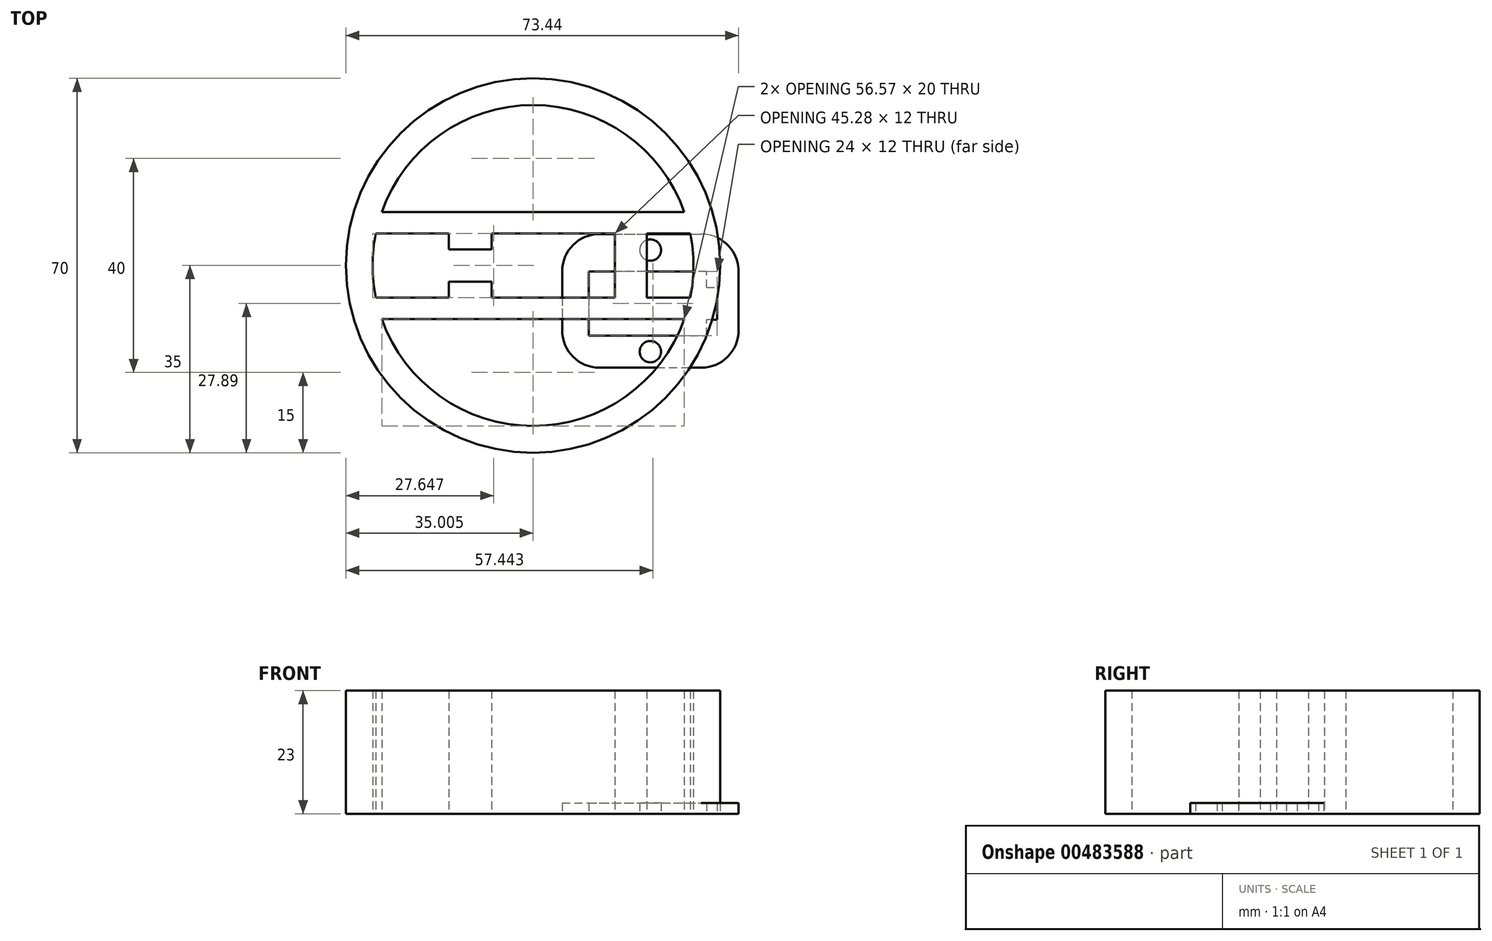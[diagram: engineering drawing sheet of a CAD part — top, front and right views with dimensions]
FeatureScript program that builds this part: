
annotation { "Feature Type Name" : "Feature", "Feature Type Description" : "" }
export const myFeature = defineFeature(function(context is Context, id is Id, definition is map)
    precondition{}
    {
        {
            var Q0;
            Q0=qCreatedBy(makeId("Top.planeOp"),FACE);
            var sketch = newSketch(context, id + "F0", { "sketchPlane" : qUnion([Q0])});
            skLineSegment(sketch, "E0.bottom", {"start": v(4.5, 11.89) * mm, "end": v(23.5, 11.89) * mm});
            skLineSegment(sketch, "E0.top", {"start": v(4.5, -13.11) * mm, "end": v(23.5, -13.11) * mm});
            skLineSegment(sketch, "E0.left", {"start": v(-2.5, 4.89) * mm, "end": v(-2.5, -6.11) * mm});
            skLineSegment(sketch, "E0.right", {"start": v(30.5, 4.89) * mm, "end": v(30.5, -6.11) * mm});
            skPoint(sketch, "E1.visualSharp", {"position": v(-2.5, 11.89) * mm});
            skArc(sketch, "E1.filletArc", {"start": v(4.5, 11.89) * mm, "mid": v(-0.46, 9.84) * mm, "end": v(-2.5, 4.89) * mm});
            skPoint(sketch, "E2.visualSharp", {"position": v(30.5, -13.11) * mm});
            skArc(sketch, "E2.filletArc", {"start": v(23.5, -13.11) * mm, "mid": v(28.44, -11.06) * mm, "end": v(30.5, -6.11) * mm});
            skPoint(sketch, "E3.visualSharp", {"position": v(-2.5, -13.11) * mm});
            skArc(sketch, "E3.filletArc", {"start": v(-2.5, -6.11) * mm, "mid": v(-0.46, -11.06) * mm, "end": v(4.5, -13.11) * mm});
            skPoint(sketch, "E4.visualSharp", {"position": v(30.5, 11.89) * mm});
            skArc(sketch, "E4.filletArc", {"start": v(30.5, 4.89) * mm, "mid": v(28.44, 9.84) * mm, "end": v(23.5, 11.89) * mm});
            skLineSegment(sketch, "E5", {"start": v(14, 11.89) * mm, "end": v(14, 8.89) * mm});
            skCircle(sketch, "E6", {"center": v(14, 8.89) * mm, "radius": 2 * mm});
            skLineSegment(sketch, "E7", {"start": v(14, -13.11) * mm, "end": v(14, -10.11) * mm});
            skCircle(sketch, "E8", {"center": v(14, -10.11) * mm, "radius": 2 * mm});
            skLineSegment(sketch, "E9", {"start": v(2.5, 4.89) * mm, "end": v(2.5, -7.11) * mm});
            skLineSegment(sketch, "E10", {"start": v(2.5, -7.11) * mm, "end": v(24.5, -7.11) * mm});
            skLineSegment(sketch, "E11", {"start": v(24.5, -7.11) * mm, "end": v(24.5, 4.89) * mm});
            skLineSegment(sketch, "E12", {"start": v(24.5, 4.89) * mm, "end": v(2.5, 4.89) * mm});
            skLineSegment(sketch, "E13", {"start": v(24.5, 4.89) * mm, "end": v(24.5, 1.89) * mm});
            skLineSegment(sketch, "E14", {"start": v(24.5, 1.89) * mm, "end": v(24.5, -4.11) * mm});
            skLineSegment(sketch, "E15", {"start": v(24.5, 1.89) * mm, "end": v(26.5, 1.89) * mm});
            skLineSegment(sketch, "E16", {"start": v(26.5, 1.89) * mm, "end": v(26.5, -4.11) * mm});
            skLineSegment(sketch, "E17", {"start": v(26.5, -4.11) * mm, "end": v(24.5, -4.11) * mm});
            skSolve(sketch);
        }
        {
            var Q0;
            Q0 = qSketchRegion(id + "F0", true);
            extrude(context, id + "F1", {"entities" : qUnion([Q0]), "depth" : 2 * mm});
        }
        {
            var Q0;
            Q0=qCreatedBy(makeId("Top.planeOp"),FACE);
            var sketch = newSketch(context, id + "F2", { "sketchPlane" : qUnion([Q0])});
            skCircle(sketch, "E18", {"center": v(-7.95, 6) * mm, "radius": 35 * mm});
            skArc(sketch, "E19", {"start": v(-37.34, 12) * mm, "mid": v(-37.95, 6) * mm, "end": v(-37.34, 0) * mm});
            skLineSegment(sketch, "E20", {"start": v(-36.23, 16) * mm, "end": v(20.34, 16) * mm});
            skLineSegment(sketch, "E21", {"start": v(-36.23, -4) * mm, "end": v(20.34, -4) * mm});
            skLineSegment(sketch, "E22", {"start": v(20.34, 0) * mm, "end": v(13.34, 0) * mm});
            skLineSegment(sketch, "E23", {"start": v(13.34, 0) * mm, "end": v(13.34, 12) * mm});
            skLineSegment(sketch, "E24", {"start": v(13.34, 12) * mm, "end": v(20.34, 12) * mm});
            skLineSegment(sketch, "E25", {"start": v(20.34, 12) * mm, "end": v(21.45, 12) * mm});
            skLineSegment(sketch, "E26", {"start": v(20.34, 0) * mm, "end": v(21.45, 0) * mm});
            skLineSegment(sketch, "E27", {"start": v(7.34, 0) * mm, "end": v(-15.66, 0) * mm});
            skLineSegment(sketch, "E28", {"start": v(-15.66, 0) * mm, "end": v(-15.66, 3) * mm});
            skLineSegment(sketch, "E29", {"start": v(-15.66, 3) * mm, "end": v(-23.66, 3) * mm});
            skLineSegment(sketch, "E30", {"start": v(7.34, 0) * mm, "end": v(7.34, 12) * mm});
            skLineSegment(sketch, "E31", {"start": v(7.34, 12) * mm, "end": v(-15.66, 12) * mm});
            skLineSegment(sketch, "E32", {"start": v(-15.66, 12) * mm, "end": v(-15.66, 9) * mm});
            skLineSegment(sketch, "E33", {"start": v(-15.66, 9) * mm, "end": v(-23.66, 9) * mm});
            skLineSegment(sketch, "E34", {"start": v(-23.66, 9) * mm, "end": v(-23.66, 12) * mm});
            skLineSegment(sketch, "E35", {"start": v(-23.66, 12) * mm, "end": v(-37.34, 12) * mm});
            skLineSegment(sketch, "E36", {"start": v(-23.66, 3) * mm, "end": v(-23.66, 0) * mm});
            skLineSegment(sketch, "E37", {"start": v(-23.66, 0) * mm, "end": v(-37.34, 0) * mm});
            skArc(sketch, "E38.trimOffspring", {"start": v(-36.23, -4) * mm, "mid": v(-7.95, -24) * mm, "end": v(20.34, -4) * mm});
            skArc(sketch, "E39.trimOffspring", {"start": v(20.34, 16) * mm, "mid": v(-7.95, 36) * mm, "end": v(-36.23, 16) * mm});
            skArc(sketch, "E40.trimOffspring", {"start": v(21.45, 0) * mm, "mid": v(22.05, 6) * mm, "end": v(21.45, 12) * mm});
            skSolve(sketch);
        }
        {
            var Q0;
            Q0=makeQuery(id+"F2.imprint","IMPRINT",FACE,{"disambiguationData":[TD([[makeQuery(id+"F2.imprint","IMPRINT",EDGE,{"derivedFrom":sQuery(id+"F2.wireOp",EDGE,"E18")}),1.0]])]});
            extrude(context, id + "F3", {"entities" : qUnion([Q0]), "depth" : 23 * mm});
        }
    });
